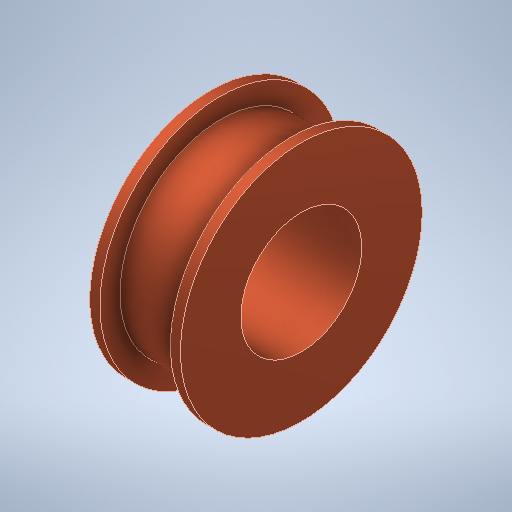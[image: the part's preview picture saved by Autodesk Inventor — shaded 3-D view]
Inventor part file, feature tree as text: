
AUTODESK INVENTOR PART (.ipt)
format: ipt  version: 2025.1 (Build 291241000, 241)  size: 276,992 bytes
history: native  units: mm
features: sketch x2, revolve x1, hole x1
ambient origin geometry x8: Origin, YZ Plane, XZ Plane, XY Plane, X Axis, Y Axis, Z Axis, Center Point
bodies: Solid1 (feature_tree)
feature tree (4):
  revolve  "Revolution1"  [1 undecoded]
  hole  "Hole1"  [1 undecoded]
  sketch  "Sketch1"  dims[d1=9.0mm d2=7.0mm]
  sketch  "Sketch2"  dims[d3=20.0mm d4=24.0mm d5=90.0deg d6=12.0mm d7=15.0mm d8=4.0mm d9=2.0mm d10=90.0deg d11=15.0mm d12=0.0mm d13=1.0mm]
note: 2 required parameter values undecoded (feature->parameter linkage not recoverable at this tier; creation-order binding heuristic only, values carry confidence <= 0.55)